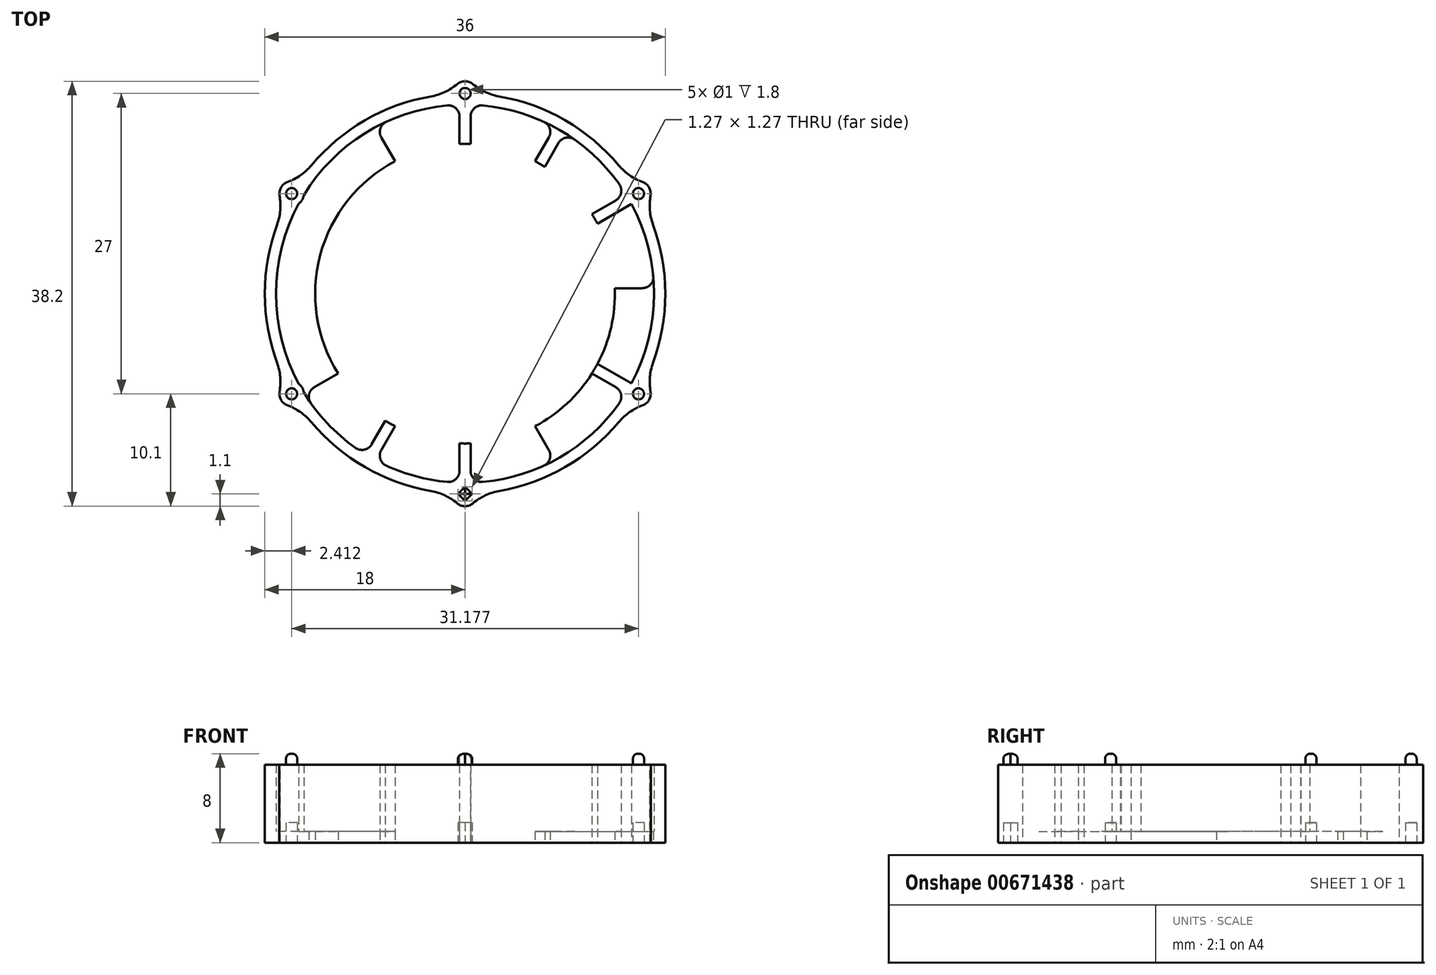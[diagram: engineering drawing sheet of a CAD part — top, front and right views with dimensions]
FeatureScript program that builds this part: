
annotation { "Feature Type Name" : "Feature", "Feature Type Description" : "" }
export const myFeature = defineFeature(function(context is Context, id is Id, definition is map)
    precondition{}
    {
        {
            var Q0;
            Q0=qCreatedBy(makeId("Top.planeOp"),FACE);
            var sketch = newSketch(context, id + "F0", { "sketchPlane" : qUnion([Q0])});
            skCircle(sketch, "E0", {"center": v(0, 0) * mm, "radius": 18 * mm});
            skCircle(sketch, "E1.0", {"center": v(0, 0) * mm, "radius": 17 * mm});
            skLineSegment(sketch, "E2.bottom", {"start": v(8.56, 15.83) * mm, "end": v(9.43, 15.33) * mm});
            skLineSegment(sketch, "E2.top", {"start": v(-9.43, -15.33) * mm, "end": v(-8.56, -15.83) * mm});
            skLineSegment(sketch, "E2.left", {"start": v(8.56, 15.83) * mm, "end": v(-9.43, -15.33) * mm});
            skLineSegment(sketch, "E2.right", {"start": v(9.43, 15.33) * mm, "end": v(-8.56, -15.83) * mm});
            skLineSegment(sketch, "E3.bottom", {"start": v(15.33, 9.43) * mm, "end": v(15.83, 8.56) * mm});
            skLineSegment(sketch, "E3.top", {"start": v(-15.83, -8.56) * mm, "end": v(-15.33, -9.43) * mm});
            skLineSegment(sketch, "E3.left", {"start": v(15.33, 9.43) * mm, "end": v(-15.83, -8.56) * mm});
            skLineSegment(sketch, "E3.right", {"start": v(15.83, 8.56) * mm, "end": v(-15.33, -9.43) * mm});
            skLineSegment(sketch, "E4", {"start": v(-38.35, 0) * mm, "end": v(39.17, 0) * mm, "construction": true});
            skLineSegment(sketch, "E5", {"start": v(0, 42.5) * mm, "end": v(0, -42.47) * mm, "construction": true});
            skLineSegment(sketch, "E6.bottom", {"start": v(-18, 0.5) * mm, "end": v(18, 0.5) * mm});
            skLineSegment(sketch, "E6.top", {"start": v(-18, -0.5) * mm, "end": v(18, -0.5) * mm});
            skLineSegment(sketch, "E6.left", {"start": v(-18, 0.5) * mm, "end": v(-18, -0.5) * mm});
            skLineSegment(sketch, "E6.right", {"start": v(18, 0.5) * mm, "end": v(18, -0.5) * mm});
            skLineSegment(sketch, "E7.bottom", {"start": v(-15.33, 9.43) * mm, "end": v(15.83, -8.56) * mm});
            skLineSegment(sketch, "E7.top", {"start": v(-15.83, 8.56) * mm, "end": v(15.33, -9.43) * mm});
            skLineSegment(sketch, "E7.left", {"start": v(-15.33, 9.43) * mm, "end": v(-15.83, 8.56) * mm});
            skLineSegment(sketch, "E7.right", {"start": v(15.83, -8.56) * mm, "end": v(15.33, -9.43) * mm});
            skLineSegment(sketch, "E8.bottom", {"start": v(-0.5, 18) * mm, "end": v(0.5, 18) * mm});
            skLineSegment(sketch, "E8.top", {"start": v(-0.5, -18) * mm, "end": v(0.5, -18) * mm});
            skLineSegment(sketch, "E8.left", {"start": v(-0.5, 18) * mm, "end": v(-0.5, -18) * mm});
            skLineSegment(sketch, "E8.right", {"start": v(0.5, 18) * mm, "end": v(0.5, -18) * mm});
            skLineSegment(sketch, "E9.bottom", {"start": v(-9.43, 15.33) * mm, "end": v(-8.56, 15.83) * mm});
            skLineSegment(sketch, "E9.top", {"start": v(8.56, -15.83) * mm, "end": v(9.43, -15.33) * mm});
            skLineSegment(sketch, "E9.left", {"start": v(-9.43, 15.33) * mm, "end": v(8.56, -15.83) * mm});
            skLineSegment(sketch, "E9.right", {"start": v(-8.56, 15.83) * mm, "end": v(9.43, -15.33) * mm});
            skCircle(sketch, "E10", {"center": v(0, 0) * mm, "radius": 13.47 * mm});
            skSolve(sketch);
        }
        {
            var Q0;
            Q0=qCreatedBy(makeId("Top.planeOp"),FACE);
            var sketch = newSketch(context, id + "F1", { "sketchPlane" : qUnion([Q0])});
            skCircle(sketch, "E11", {"center": v(0, 0) * mm, "radius": 18 * mm});
            skCircle(sketch, "E12", {"center": v(0, 0) * mm, "radius": 17 * mm});
            skSolve(sketch);
        }
        {
            var Q0;
            Q0=makeQuery(id+"F1.imprint","IMPRINT",FACE,{"disambiguationData":[TD([[makeQuery(id+"F1.imprint","IMPRINT",EDGE,{"derivedFrom":sQuery(id+"F1.wireOp",EDGE,"E11")}),1.0]])]});
            extrude(context, id + "F2", {"entities" : qUnion([Q0]), "depth" : 7 * mm, "offsetDistance" : 25 * mm});
        }
        {
            var Q0;
            {var subQ0=sQuery(id+"F0.wireOp",EDGE,"E8.left");var subQ1=sQuery(id+"F0.wireOp",EDGE,"E1.0");var subQ2=makeQuery(id+"F0.imprint","INTERSECT",VERTEX,{"disambiguationData":[OD(1.0)],"derivedFrom":[subQ1,subQ0]});Q0=makeQuery(id+"F0.imprint","IMPRINT",FACE,{"disambiguationData":[TD([[makeQuery(id+"F0.imprint","IMPRINT",EDGE,{"disambiguationData":[TD([[subQ2,-1.0]])],"derivedFrom":subQ1}),1.0]])]});}
            var Q1;
            {var subQ0=sQuery(id+"F0.wireOp",EDGE,"E8.right");var subQ1=sQuery(id+"F0.wireOp",EDGE,"E1.0");var subQ2=makeQuery(id+"F0.imprint","INTERSECT",VERTEX,{"disambiguationData":[OD(0.0)],"derivedFrom":[subQ1,subQ0]});Q1=makeQuery(id+"F0.imprint","IMPRINT",FACE,{"disambiguationData":[TD([[makeQuery(id+"F0.imprint","IMPRINT",EDGE,{"disambiguationData":[TD([[subQ2,-1.0]])],"derivedFrom":subQ1}),1.0]])]});}
            var Q2;
            {var subQ0=sQuery(id+"F0.wireOp",EDGE,"E3.right");var subQ1=sQuery(id+"F0.wireOp",EDGE,"E1.0");var subQ2=makeQuery(id+"F0.imprint","INTERSECT",VERTEX,{"disambiguationData":[OD(0.0)],"derivedFrom":[subQ1,subQ0]});Q2=makeQuery(id+"F0.imprint","IMPRINT",FACE,{"disambiguationData":[TD([[makeQuery(id+"F0.imprint","IMPRINT",EDGE,{"disambiguationData":[TD([[subQ2,-1.0]])],"derivedFrom":subQ1}),1.0]])]});}
            var Q3;
            {var subQ0=sQuery(id+"F0.wireOp",EDGE,"E7.top");var subQ1=sQuery(id+"F0.wireOp",EDGE,"E1.0");var subQ2=makeQuery(id+"F0.imprint","INTERSECT",VERTEX,{"disambiguationData":[OD(1.0)],"derivedFrom":[subQ1,subQ0]});Q3=makeQuery(id+"F0.imprint","IMPRINT",FACE,{"disambiguationData":[TD([[makeQuery(id+"F0.imprint","IMPRINT",EDGE,{"disambiguationData":[TD([[subQ2,-1.0]])],"derivedFrom":subQ1}),1.0]])]});}
            var Q4;
            {var subQ0=sQuery(id+"F0.wireOp",EDGE,"E2.left");var subQ1=sQuery(id+"F0.wireOp",EDGE,"E1.0");var subQ2=makeQuery(id+"F0.imprint","INTERSECT",VERTEX,{"disambiguationData":[OD(1.0)],"derivedFrom":[subQ1,subQ0]});Q4=makeQuery(id+"F0.imprint","IMPRINT",FACE,{"disambiguationData":[TD([[makeQuery(id+"F0.imprint","IMPRINT",EDGE,{"disambiguationData":[TD([[subQ2,-1.0]])],"derivedFrom":subQ1}),1.0]])]});}
            extrude(context, id + "F3", {"entities" : qUnion([Q0, Q1, Q2, Q3, Q4]), "operationType" : NewBodyOperationType.ADD, "depth" : 7 * mm, "offsetDistance" : 25 * mm});
        }
        {
            var Q0;
            Q0=makeQuery(id+"F1.imprint","IMPRINT",FACE,{"disambiguationData":[TD([[makeQuery(id+"F1.imprint","IMPRINT",EDGE,{"derivedFrom":sQuery(id+"F1.wireOp",EDGE,"E11")}),1.0]])]});
            var Q1;
            Q1=makeQuery(id+"F1.imprint","IMPRINT",FACE,{"disambiguationData":[TD([[makeQuery(id+"F1.imprint","IMPRINT",EDGE,{"derivedFrom":sQuery(id+"F1.wireOp",EDGE,"E12")}),1.0]])]});
            extrude(context, id + "F4", {"entities" : qUnion([Q0, Q1]), "operationType" : NewBodyOperationType.ADD, "depth" : 1 * mm, "offsetDistance" : 25 * mm});
        }
        {
            var Q0;
            Q0=qCreatedBy(makeId("Top.planeOp"),FACE);
            var sketch = newSketch(context, id + "F5", { "sketchPlane" : qUnion([Q0])});
            skCircle(sketch, "E13", {"center": v(0, 0) * mm, "radius": 18 * mm});
            skLineSegment(sketch, "E14", {"start": v(0, 18) * mm, "end": v(0, -18) * mm, "construction": true});
            skLineSegment(sketch, "E15", {"start": v(15.59, 9) * mm, "end": v(0, 0) * mm, "construction": true});
            skLineSegment(sketch, "E16", {"start": v(9, 15.59) * mm, "end": v(0, 0) * mm, "construction": true});
            skLineSegment(sketch, "E17", {"start": v(0, 0) * mm, "end": v(18, 0) * mm, "construction": true});
            skLineSegment(sketch, "E18", {"start": v(0, 0) * mm, "end": v(15.59, -9) * mm, "construction": true});
            skLineSegment(sketch, "E19", {"start": v(0, 0) * mm, "end": v(9, -15.59) * mm, "construction": true});
            skLineSegment(sketch, "E20", {"start": v(0, 0) * mm, "end": v(-9, 15.59) * mm, "construction": true});
            skLineSegment(sketch, "E21", {"start": v(0, 0) * mm, "end": v(-15.59, 9) * mm, "construction": true});
            skLineSegment(sketch, "E22", {"start": v(0, 0) * mm, "end": v(-18, 0) * mm, "construction": true});
            skLineSegment(sketch, "E23", {"start": v(0, 0) * mm, "end": v(-15.59, -9) * mm, "construction": true});
            skLineSegment(sketch, "E24", {"start": v(0, 0) * mm, "end": v(-9, -15.59) * mm, "construction": true});
            skCircle(sketch, "E25", {"center": v(0, 18) * mm, "radius": 1.1 * mm});
            skCircle(sketch, "E26", {"center": v(15.59, 9) * mm, "radius": 1.1 * mm});
            skCircle(sketch, "E27", {"center": v(15.59, -9) * mm, "radius": 1.1 * mm});
            skCircle(sketch, "E28", {"center": v(0, -18) * mm, "radius": 1.1 * mm});
            skCircle(sketch, "E29", {"center": v(-15.59, -9) * mm, "radius": 1.1 * mm});
            skCircle(sketch, "E30", {"center": v(-15.59, 9) * mm, "radius": 1.1 * mm});
            skCircle(sketch, "E31", {"center": v(-15.59, 9) * mm, "radius": 0.5 * mm});
            skCircle(sketch, "E32", {"center": v(0, 18) * mm, "radius": 0.5 * mm});
            skCircle(sketch, "E33", {"center": v(15.59, 9) * mm, "radius": 0.5 * mm});
            skCircle(sketch, "E34", {"center": v(15.59, -9) * mm, "radius": 0.5 * mm});
            skCircle(sketch, "E35", {"center": v(-15.59, -9) * mm, "radius": 0.5 * mm});
            skLineSegment(sketch, "E36.bottom", {"start": v(0.64, -18) * mm, "end": v(0, -18.64) * mm});
            skLineSegment(sketch, "E36.top", {"start": v(0, -17.36) * mm, "end": v(-0.64, -18) * mm});
            skLineSegment(sketch, "E36.left", {"start": v(0.64, -18) * mm, "end": v(0, -17.36) * mm});
            skLineSegment(sketch, "E36.right", {"start": v(0, -18.64) * mm, "end": v(-0.64, -18) * mm});
            skSolve(sketch);
        }
        {
            var Q0;
            {var subQ0=sQuery(id+"F5.wireOp",EDGE,"E30");var subQ1=sQuery(id+"F5.wireOp",EDGE,"E13");var subQ2=makeQuery(id+"F5.imprint","INTERSECT",VERTEX,{"disambiguationData":[OD(0.0)],"derivedFrom":[subQ1,subQ0]});Q0=makeQuery(id+"F5.imprint","IMPRINT",FACE,{"disambiguationData":[TD([[makeQuery(id+"F5.imprint","IMPRINT",EDGE,{"disambiguationData":[TD([[subQ2,-1.0]])],"derivedFrom":subQ1}),1.0]])]});}
            var Q1;
            {var subQ0=sQuery(id+"F5.wireOp",EDGE,"E30");var subQ1=sQuery(id+"F5.wireOp",EDGE,"E13");var subQ2=makeQuery(id+"F5.imprint","INTERSECT",VERTEX,{"disambiguationData":[OD(0.0)],"derivedFrom":[subQ1,subQ0]});Q1=makeQuery(id+"F5.imprint","IMPRINT",FACE,{"disambiguationData":[TD([[makeQuery(id+"F5.imprint","IMPRINT",EDGE,{"disambiguationData":[TD([[subQ2,-1.0]])],"derivedFrom":subQ1}),-1.0]])]});}
            var Q2;
            {var subQ0=sQuery(id+"F5.wireOp",EDGE,"E25");var subQ1=sQuery(id+"F5.wireOp",EDGE,"E13");var subQ2=makeQuery(id+"F5.imprint","INTERSECT",VERTEX,{"disambiguationData":[OD(0.0)],"derivedFrom":[subQ1,subQ0]});Q2=makeQuery(id+"F5.imprint","IMPRINT",FACE,{"disambiguationData":[TD([[makeQuery(id+"F5.imprint","IMPRINT",EDGE,{"disambiguationData":[TD([[subQ2,-1.0]])],"derivedFrom":subQ1}),1.0]])]});}
            var Q3;
            {var subQ0=sQuery(id+"F5.wireOp",EDGE,"E25");var subQ1=sQuery(id+"F5.wireOp",EDGE,"E13");var subQ2=makeQuery(id+"F5.imprint","INTERSECT",VERTEX,{"disambiguationData":[OD(0.0)],"derivedFrom":[subQ1,subQ0]});Q3=makeQuery(id+"F5.imprint","IMPRINT",FACE,{"disambiguationData":[TD([[makeQuery(id+"F5.imprint","IMPRINT",EDGE,{"disambiguationData":[TD([[subQ2,-1.0]])],"derivedFrom":subQ1}),-1.0]])]});}
            var Q4;
            {var subQ0=sQuery(id+"F5.wireOp",EDGE,"E26");var subQ1=sQuery(id+"F5.wireOp",EDGE,"E13");var subQ2=makeQuery(id+"F5.imprint","INTERSECT",VERTEX,{"disambiguationData":[OD(0.0)],"derivedFrom":[subQ1,subQ0]});Q4=makeQuery(id+"F5.imprint","IMPRINT",FACE,{"disambiguationData":[TD([[makeQuery(id+"F5.imprint","IMPRINT",EDGE,{"disambiguationData":[TD([[subQ2,-1.0]])],"derivedFrom":subQ1}),-1.0]])]});}
            var Q5;
            {var subQ0=sQuery(id+"F5.wireOp",EDGE,"E26");var subQ1=sQuery(id+"F5.wireOp",EDGE,"E13");var subQ2=makeQuery(id+"F5.imprint","INTERSECT",VERTEX,{"disambiguationData":[OD(0.0)],"derivedFrom":[subQ1,subQ0]});Q5=makeQuery(id+"F5.imprint","IMPRINT",FACE,{"disambiguationData":[TD([[makeQuery(id+"F5.imprint","IMPRINT",EDGE,{"disambiguationData":[TD([[subQ2,-1.0]])],"derivedFrom":subQ1}),1.0]])]});}
            var Q6;
            {var subQ0=sQuery(id+"F5.wireOp",EDGE,"E29");var subQ1=sQuery(id+"F5.wireOp",EDGE,"E13");var subQ2=makeQuery(id+"F5.imprint","INTERSECT",VERTEX,{"disambiguationData":[OD(0.0)],"derivedFrom":[subQ1,subQ0]});Q6=makeQuery(id+"F5.imprint","IMPRINT",FACE,{"disambiguationData":[TD([[makeQuery(id+"F5.imprint","IMPRINT",EDGE,{"disambiguationData":[TD([[subQ2,-1.0]])],"derivedFrom":subQ1}),1.0]])]});}
            var Q7;
            {var subQ0=sQuery(id+"F5.wireOp",EDGE,"E29");var subQ1=sQuery(id+"F5.wireOp",EDGE,"E13");var subQ2=makeQuery(id+"F5.imprint","INTERSECT",VERTEX,{"disambiguationData":[OD(0.0)],"derivedFrom":[subQ1,subQ0]});Q7=makeQuery(id+"F5.imprint","IMPRINT",FACE,{"disambiguationData":[TD([[makeQuery(id+"F5.imprint","IMPRINT",EDGE,{"disambiguationData":[TD([[subQ2,-1.0]])],"derivedFrom":subQ1}),-1.0]])]});}
            var Q8;
            {var subQ3=sQuery(id+"F5.wireOp",EDGE,"E13");var subQ5=sQuery(id+"F5.wireOp",EDGE,"E28");var subQ6=makeQuery(id+"F5.imprint","INTERSECT",VERTEX,{"disambiguationData":[OD(0.0)],"derivedFrom":[subQ3,subQ5]});Q8=makeQuery(id+"F5.imprint","IMPRINT",FACE,{"disambiguationData":[TD([[makeQuery(id+"F5.imprint","IMPRINT",EDGE,{"disambiguationData":[TD([[subQ6,-1.0]])],"derivedFrom":subQ3}),1.0]])]});}
            var Q9;
            {var subQ6=sQuery(id+"F5.wireOp",EDGE,"E36.bottom");Q9=makeQuery(id+"F5.imprint","IMPRINT",FACE,{"disambiguationData":[TD([[makeQuery(id+"F5.imprint","IMPRINT",EDGE,{"derivedFrom":subQ6}),1.0]])]});}
            var Q10;
            {var subQ0=sQuery(id+"F5.wireOp",EDGE,"E27");var subQ1=sQuery(id+"F5.wireOp",EDGE,"E13");var subQ2=makeQuery(id+"F5.imprint","INTERSECT",VERTEX,{"disambiguationData":[OD(0.0)],"derivedFrom":[subQ1,subQ0]});Q10=makeQuery(id+"F5.imprint","IMPRINT",FACE,{"disambiguationData":[TD([[makeQuery(id+"F5.imprint","IMPRINT",EDGE,{"disambiguationData":[TD([[subQ2,-1.0]])],"derivedFrom":subQ1}),-1.0]])]});}
            var Q11;
            {var subQ0=sQuery(id+"F5.wireOp",EDGE,"E27");var subQ1=sQuery(id+"F5.wireOp",EDGE,"E13");var subQ2=makeQuery(id+"F5.imprint","INTERSECT",VERTEX,{"disambiguationData":[OD(0.0)],"derivedFrom":[subQ1,subQ0]});Q11=makeQuery(id+"F5.imprint","IMPRINT",FACE,{"disambiguationData":[TD([[makeQuery(id+"F5.imprint","IMPRINT",EDGE,{"disambiguationData":[TD([[subQ2,-1.0]])],"derivedFrom":subQ1}),1.0]])]});}
            var Q12;
            {var subQ0=sQuery(id+"F5.wireOp",EDGE,"E31");var subQ1=sQuery(id+"F5.wireOp",EDGE,"E13");var subQ2=makeQuery(id+"F5.imprint","INTERSECT",VERTEX,{"disambiguationData":[OD(0.0)],"derivedFrom":[subQ1,subQ0]});Q12=makeQuery(id+"F5.imprint","IMPRINT",FACE,{"disambiguationData":[TD([[makeQuery(id+"F5.imprint","IMPRINT",EDGE,{"disambiguationData":[TD([[subQ2,-1.0]])],"derivedFrom":subQ1}),1.0]])]});}
            var Q13;
            {var subQ0=sQuery(id+"F5.wireOp",EDGE,"E31");var subQ1=sQuery(id+"F5.wireOp",EDGE,"E13");var subQ2=makeQuery(id+"F5.imprint","INTERSECT",VERTEX,{"disambiguationData":[OD(0.0)],"derivedFrom":[subQ1,subQ0]});Q13=makeQuery(id+"F5.imprint","IMPRINT",FACE,{"disambiguationData":[TD([[makeQuery(id+"F5.imprint","IMPRINT",EDGE,{"disambiguationData":[TD([[subQ2,-1.0]])],"derivedFrom":subQ1}),-1.0]])]});}
            var Q14;
            {var subQ0=sQuery(id+"F5.wireOp",EDGE,"E32");var subQ1=sQuery(id+"F5.wireOp",EDGE,"E13");var subQ2=makeQuery(id+"F5.imprint","INTERSECT",VERTEX,{"disambiguationData":[OD(0.0)],"derivedFrom":[subQ1,subQ0]});Q14=makeQuery(id+"F5.imprint","IMPRINT",FACE,{"disambiguationData":[TD([[makeQuery(id+"F5.imprint","IMPRINT",EDGE,{"disambiguationData":[TD([[subQ2,-1.0]])],"derivedFrom":subQ1}),-1.0]])]});}
            var Q15;
            {var subQ0=sQuery(id+"F5.wireOp",EDGE,"E32");var subQ1=sQuery(id+"F5.wireOp",EDGE,"E13");var subQ2=makeQuery(id+"F5.imprint","INTERSECT",VERTEX,{"disambiguationData":[OD(0.0)],"derivedFrom":[subQ1,subQ0]});Q15=makeQuery(id+"F5.imprint","IMPRINT",FACE,{"disambiguationData":[TD([[makeQuery(id+"F5.imprint","IMPRINT",EDGE,{"disambiguationData":[TD([[subQ2,-1.0]])],"derivedFrom":subQ1}),1.0]])]});}
            var Q16;
            {var subQ0=sQuery(id+"F5.wireOp",EDGE,"E33");var subQ1=sQuery(id+"F5.wireOp",EDGE,"E13");var subQ2=makeQuery(id+"F5.imprint","INTERSECT",VERTEX,{"disambiguationData":[OD(0.0)],"derivedFrom":[subQ1,subQ0]});Q16=makeQuery(id+"F5.imprint","IMPRINT",FACE,{"disambiguationData":[TD([[makeQuery(id+"F5.imprint","IMPRINT",EDGE,{"disambiguationData":[TD([[subQ2,-1.0]])],"derivedFrom":subQ1}),-1.0]])]});}
            var Q17;
            {var subQ0=sQuery(id+"F5.wireOp",EDGE,"E33");var subQ1=sQuery(id+"F5.wireOp",EDGE,"E13");var subQ2=makeQuery(id+"F5.imprint","INTERSECT",VERTEX,{"disambiguationData":[OD(0.0)],"derivedFrom":[subQ1,subQ0]});Q17=makeQuery(id+"F5.imprint","IMPRINT",FACE,{"disambiguationData":[TD([[makeQuery(id+"F5.imprint","IMPRINT",EDGE,{"disambiguationData":[TD([[subQ2,-1.0]])],"derivedFrom":subQ1}),1.0]])]});}
            var Q18;
            {var subQ0=sQuery(id+"F5.wireOp",EDGE,"E34");var subQ1=sQuery(id+"F5.wireOp",EDGE,"E13");var subQ2=makeQuery(id+"F5.imprint","INTERSECT",VERTEX,{"disambiguationData":[OD(0.0)],"derivedFrom":[subQ1,subQ0]});Q18=makeQuery(id+"F5.imprint","IMPRINT",FACE,{"disambiguationData":[TD([[makeQuery(id+"F5.imprint","IMPRINT",EDGE,{"disambiguationData":[TD([[subQ2,-1.0]])],"derivedFrom":subQ1}),-1.0]])]});}
            var Q19;
            {var subQ0=sQuery(id+"F5.wireOp",EDGE,"E34");var subQ1=sQuery(id+"F5.wireOp",EDGE,"E13");var subQ2=makeQuery(id+"F5.imprint","INTERSECT",VERTEX,{"disambiguationData":[OD(0.0)],"derivedFrom":[subQ1,subQ0]});Q19=makeQuery(id+"F5.imprint","IMPRINT",FACE,{"disambiguationData":[TD([[makeQuery(id+"F5.imprint","IMPRINT",EDGE,{"disambiguationData":[TD([[subQ2,-1.0]])],"derivedFrom":subQ1}),1.0]])]});}
            var Q20;
            {var subQ1=sQuery(id+"F5.wireOp",EDGE,"E36.bottom");Q20=makeQuery(id+"F5.imprint","IMPRINT",FACE,{"disambiguationData":[TD([[makeQuery(id+"F5.imprint","IMPRINT",EDGE,{"derivedFrom":subQ1}),-1.0]])]});}
            var Q21;
            {var subQ0=sQuery(id+"F5.wireOp",EDGE,"E35");var subQ1=sQuery(id+"F5.wireOp",EDGE,"E13");var subQ2=makeQuery(id+"F5.imprint","INTERSECT",VERTEX,{"disambiguationData":[OD(0.0)],"derivedFrom":[subQ1,subQ0]});Q21=makeQuery(id+"F5.imprint","IMPRINT",FACE,{"disambiguationData":[TD([[makeQuery(id+"F5.imprint","IMPRINT",EDGE,{"disambiguationData":[TD([[subQ2,-1.0]])],"derivedFrom":subQ1}),-1.0]])]});}
            var Q22;
            {var subQ0=sQuery(id+"F5.wireOp",EDGE,"E35");var subQ1=sQuery(id+"F5.wireOp",EDGE,"E13");var subQ2=makeQuery(id+"F5.imprint","INTERSECT",VERTEX,{"disambiguationData":[OD(0.0)],"derivedFrom":[subQ1,subQ0]});Q22=makeQuery(id+"F5.imprint","IMPRINT",FACE,{"disambiguationData":[TD([[makeQuery(id+"F5.imprint","IMPRINT",EDGE,{"disambiguationData":[TD([[subQ2,-1.0]])],"derivedFrom":subQ1}),1.0]])]});}
            var Q23;
            {var subQ0=sQuery(id+"F5.wireOp",EDGE,"E36.top");var subQ1=sQuery(id+"F5.wireOp",EDGE,"E13");var subQ2=makeQuery(id+"F5.imprint","INTERSECT",VERTEX,{"derivedFrom":[subQ1,subQ0]});Q23=makeQuery(id+"F5.imprint","IMPRINT",FACE,{"disambiguationData":[TD([[makeQuery(id+"F5.imprint","IMPRINT",EDGE,{"disambiguationData":[TD([[subQ2,-1.0]])],"derivedFrom":subQ1}),1.0]])]});}
            extrude(context, id + "F6", {"entities" : qUnion([Q0, Q1, Q2, Q3, Q4, Q5, Q6, Q7, Q8, Q9, Q10, Q11, Q12, Q13, Q14, Q15, Q16, Q17, Q18, Q19, Q20, Q21, Q22, Q23]), "operationType" : NewBodyOperationType.ADD, "depth" : 7 * mm, "offsetDistance" : 25 * mm});
        }
        {
            var Q0;
            {var subQ0=sQuery(id+"F0.wireOp",EDGE,"E8.right");var subQ1=sQuery(id+"F0.wireOp",EDGE,"E1.0");Q0=makeQuery(id+"F3.opExtrude","SWEPT_EDGE",EDGE,{"disambiguationData":[OSD([subQ1,subQ0]),TDD([makeQuery(id+"F0.imprint","INTERSECT",VERTEX,{"disambiguationData":[OD(1.0)],"derivedFrom":[subQ1,subQ0]})])]});}
            var Q1;
            {var subQ0=sQuery(id+"F0.wireOp",EDGE,"E2.left");var subQ1=sQuery(id+"F0.wireOp",EDGE,"E1.0");Q1=makeQuery(id+"F3.opExtrude","SWEPT_EDGE",EDGE,{"disambiguationData":[OSD([subQ1,subQ0]),TDD([makeQuery(id+"F0.imprint","INTERSECT",VERTEX,{"disambiguationData":[OD(1.0)],"derivedFrom":[subQ1,subQ0]})])]});}
            var Q2;
            {var subQ0=sQuery(id+"F0.wireOp",EDGE,"E3.left");var subQ1=sQuery(id+"F0.wireOp",EDGE,"E1.0");Q2=makeQuery(id+"F3.opExtrude","SWEPT_EDGE",EDGE,{"disambiguationData":[OSD([subQ1,subQ0]),TDD([makeQuery(id+"F0.imprint","INTERSECT",VERTEX,{"disambiguationData":[OD(1.0)],"derivedFrom":[subQ1,subQ0]})])]});}
            var Q3;
            {var subQ0=sQuery(id+"F0.wireOp",EDGE,"E6.bottom");var subQ1=sQuery(id+"F0.wireOp",EDGE,"E1.0");Q3=makeQuery(id+"F3.opExtrude","SWEPT_EDGE",EDGE,{"disambiguationData":[OSD([subQ1,subQ0]),TDD([makeQuery(id+"F0.imprint","INTERSECT",VERTEX,{"disambiguationData":[OD(1.0)],"derivedFrom":[subQ1,subQ0]})])]});}
            var Q4;
            {var subQ0=sQuery(id+"F0.wireOp",EDGE,"E9.right");var subQ1=sQuery(id+"F0.wireOp",EDGE,"E1.0");Q4=makeQuery(id+"F3.opExtrude","SWEPT_EDGE",EDGE,{"disambiguationData":[OSD([subQ1,subQ0]),TDD([makeQuery(id+"F0.imprint","INTERSECT",VERTEX,{"disambiguationData":[OD(1.0)],"derivedFrom":[subQ1,subQ0]})])]});}
            var Q5;
            {var subQ0=sQuery(id+"F0.wireOp",EDGE,"E7.bottom");var subQ1=sQuery(id+"F0.wireOp",EDGE,"E1.0");Q5=makeQuery(id+"F3.opExtrude","SWEPT_EDGE",EDGE,{"disambiguationData":[OSD([subQ1,subQ0]),TDD([makeQuery(id+"F0.imprint","INTERSECT",VERTEX,{"disambiguationData":[OD(1.0)],"derivedFrom":[subQ1,subQ0]})])]});}
            var Q6;
            {var subQ0=sQuery(id+"F0.wireOp",EDGE,"E8.left");var subQ1=sQuery(id+"F0.wireOp",EDGE,"E1.0");Q6=makeQuery(id+"F3.opExtrude","SWEPT_EDGE",EDGE,{"disambiguationData":[OSD([subQ1,subQ0]),TDD([makeQuery(id+"F0.imprint","INTERSECT",VERTEX,{"disambiguationData":[OD(0.0)],"derivedFrom":[subQ1,subQ0]})])]});}
            var Q7;
            {var subQ0=sQuery(id+"F0.wireOp",EDGE,"E2.left");var subQ1=sQuery(id+"F0.wireOp",EDGE,"E1.0");Q7=makeQuery(id+"F3.opExtrude","SWEPT_EDGE",EDGE,{"disambiguationData":[OSD([subQ1,subQ0]),TDD([makeQuery(id+"F0.imprint","INTERSECT",VERTEX,{"disambiguationData":[OD(0.0)],"derivedFrom":[subQ1,subQ0]})])]});}
            var Q8;
            {var subQ0=sQuery(id+"F0.wireOp",EDGE,"E3.left");var subQ1=sQuery(id+"F0.wireOp",EDGE,"E1.0");Q8=makeQuery(id+"F3.opExtrude","SWEPT_EDGE",EDGE,{"disambiguationData":[OSD([subQ1,subQ0]),TDD([makeQuery(id+"F0.imprint","INTERSECT",VERTEX,{"disambiguationData":[OD(0.0)],"derivedFrom":[subQ1,subQ0]})])]});}
            var Q9;
            {var subQ0=sQuery(id+"F0.wireOp",EDGE,"E6.top");var subQ1=sQuery(id+"F0.wireOp",EDGE,"E1.0");Q9=makeQuery(id+"F3.opExtrude","SWEPT_EDGE",EDGE,{"disambiguationData":[OSD([subQ1,subQ0]),TDD([makeQuery(id+"F0.imprint","INTERSECT",VERTEX,{"disambiguationData":[OD(1.0)],"derivedFrom":[subQ1,subQ0]})])]});}
            var Q10;
            {var subQ0=sQuery(id+"F0.wireOp",EDGE,"E7.top");var subQ1=sQuery(id+"F0.wireOp",EDGE,"E1.0");Q10=makeQuery(id+"F3.opExtrude","SWEPT_EDGE",EDGE,{"disambiguationData":[OSD([subQ1,subQ0]),TDD([makeQuery(id+"F0.imprint","INTERSECT",VERTEX,{"disambiguationData":[OD(0.0)],"derivedFrom":[subQ1,subQ0]})])]});}
            var Q11;
            {var subQ0=sQuery(id+"F0.wireOp",EDGE,"E6.top");var subQ1=sQuery(id+"F0.wireOp",EDGE,"E1.0");Q11=makeQuery(id+"F3.opExtrude","SWEPT_EDGE",EDGE,{"disambiguationData":[OSD([subQ1,subQ0]),TDD([makeQuery(id+"F0.imprint","INTERSECT",VERTEX,{"disambiguationData":[OD(0.0)],"derivedFrom":[subQ1,subQ0]})])]});}
            var Q12;
            {var subQ0=sQuery(id+"F0.wireOp",EDGE,"E9.left");var subQ1=sQuery(id+"F0.wireOp",EDGE,"E1.0");Q12=makeQuery(id+"F3.opExtrude","SWEPT_EDGE",EDGE,{"disambiguationData":[OSD([subQ1,subQ0]),TDD([makeQuery(id+"F0.imprint","INTERSECT",VERTEX,{"disambiguationData":[OD(0.0)],"derivedFrom":[subQ1,subQ0]})])]});}
            var Q13;
            {var subQ0=sQuery(id+"F0.wireOp",EDGE,"E8.right");var subQ1=sQuery(id+"F0.wireOp",EDGE,"E1.0");Q13=makeQuery(id+"F3.opExtrude","SWEPT_EDGE",EDGE,{"disambiguationData":[OSD([subQ1,subQ0]),TDD([makeQuery(id+"F0.imprint","INTERSECT",VERTEX,{"disambiguationData":[OD(0.0)],"derivedFrom":[subQ1,subQ0]})])]});}
            var Q14;
            {var subQ0=sQuery(id+"F0.wireOp",EDGE,"E7.bottom");var subQ1=sQuery(id+"F0.wireOp",EDGE,"E1.0");Q14=makeQuery(id+"F3.opExtrude","SWEPT_EDGE",EDGE,{"disambiguationData":[OSD([subQ1,subQ0]),TDD([makeQuery(id+"F0.imprint","INTERSECT",VERTEX,{"disambiguationData":[OD(0.0)],"derivedFrom":[subQ1,subQ0]})])]});}
            var Q15;
            {var subQ0=sQuery(id+"F0.wireOp",EDGE,"E9.right");var subQ1=sQuery(id+"F0.wireOp",EDGE,"E1.0");Q15=makeQuery(id+"F3.opExtrude","SWEPT_EDGE",EDGE,{"disambiguationData":[OSD([subQ1,subQ0]),TDD([makeQuery(id+"F0.imprint","INTERSECT",VERTEX,{"disambiguationData":[OD(0.0)],"derivedFrom":[subQ1,subQ0]})])]});}
            var Q16;
            {var subQ0=sQuery(id+"F0.wireOp",EDGE,"E3.right");var subQ1=sQuery(id+"F0.wireOp",EDGE,"E1.0");Q16=makeQuery(id+"F3.opExtrude","SWEPT_EDGE",EDGE,{"disambiguationData":[OSD([subQ1,subQ0]),TDD([makeQuery(id+"F0.imprint","INTERSECT",VERTEX,{"disambiguationData":[OD(1.0)],"derivedFrom":[subQ1,subQ0]})])]});}
            var Q17;
            {var subQ0=sQuery(id+"F0.wireOp",EDGE,"E2.right");var subQ1=sQuery(id+"F0.wireOp",EDGE,"E1.0");Q17=makeQuery(id+"F3.opExtrude","SWEPT_EDGE",EDGE,{"disambiguationData":[OSD([subQ1,subQ0]),TDD([makeQuery(id+"F0.imprint","INTERSECT",VERTEX,{"disambiguationData":[OD(1.0)],"derivedFrom":[subQ1,subQ0]})])]});}
            var Q18;
            {var subQ0=sQuery(id+"F0.wireOp",EDGE,"E3.right");var subQ1=sQuery(id+"F0.wireOp",EDGE,"E1.0");Q18=makeQuery(id+"F3.opExtrude","SWEPT_EDGE",EDGE,{"disambiguationData":[OSD([subQ1,subQ0]),TDD([makeQuery(id+"F0.imprint","INTERSECT",VERTEX,{"disambiguationData":[OD(0.0)],"derivedFrom":[subQ1,subQ0]})])]});}
            var Q19;
            {var subQ0=sQuery(id+"F0.wireOp",EDGE,"E2.right");var subQ1=sQuery(id+"F0.wireOp",EDGE,"E1.0");Q19=makeQuery(id+"F3.opExtrude","SWEPT_EDGE",EDGE,{"disambiguationData":[OSD([subQ1,subQ0]),TDD([makeQuery(id+"F0.imprint","INTERSECT",VERTEX,{"disambiguationData":[OD(0.0)],"derivedFrom":[subQ1,subQ0]})])]});}
            var Q20;
            {var subQ0=sQuery(id+"F0.wireOp",EDGE,"E8.left");var subQ1=sQuery(id+"F0.wireOp",EDGE,"E1.0");Q20=makeQuery(id+"F3.opExtrude","SWEPT_EDGE",EDGE,{"disambiguationData":[OSD([subQ1,subQ0]),TDD([makeQuery(id+"F0.imprint","INTERSECT",VERTEX,{"disambiguationData":[OD(1.0)],"derivedFrom":[subQ1,subQ0]})])]});}
            var Q21;
            {var subQ0=sQuery(id+"F0.wireOp",EDGE,"E9.left");var subQ1=sQuery(id+"F0.wireOp",EDGE,"E1.0");Q21=makeQuery(id+"F3.opExtrude","SWEPT_EDGE",EDGE,{"disambiguationData":[OSD([subQ1,subQ0]),TDD([makeQuery(id+"F0.imprint","INTERSECT",VERTEX,{"disambiguationData":[OD(1.0)],"derivedFrom":[subQ1,subQ0]})])]});}
            var Q22;
            {var subQ0=sQuery(id+"F0.wireOp",EDGE,"E7.top");var subQ1=sQuery(id+"F0.wireOp",EDGE,"E1.0");Q22=makeQuery(id+"F3.opExtrude","SWEPT_EDGE",EDGE,{"disambiguationData":[OSD([subQ1,subQ0]),TDD([makeQuery(id+"F0.imprint","INTERSECT",VERTEX,{"disambiguationData":[OD(1.0)],"derivedFrom":[subQ1,subQ0]})])]});}
            var Q23;
            {var subQ0=sQuery(id+"F0.wireOp",EDGE,"E6.bottom");var subQ1=sQuery(id+"F0.wireOp",EDGE,"E1.0");Q23=makeQuery(id+"F3.opExtrude","SWEPT_EDGE",EDGE,{"disambiguationData":[OSD([subQ1,subQ0]),TDD([makeQuery(id+"F0.imprint","INTERSECT",VERTEX,{"disambiguationData":[OD(0.0)],"derivedFrom":[subQ1,subQ0]})])]});}
            fillet(context, id + "F7", {"entities" : qUnion([Q0, Q1, Q2, Q3, Q4, Q5, Q6, Q7, Q8, Q9, Q10, Q11, Q12, Q13, Q14, Q15, Q16, Q17, Q18, Q19, Q20, Q21, Q22, Q23]), "radius" : 1 * mm, "tangentPropagation" : true, "allowEdgeOverflow" : false});
        }
        {
            var Q0;
            Q0=makeQuery(id+"F6.boolean.opBoolean","INTERSECT",EDGE,{"disambiguationData":[OD(0.0)],"derivedFrom":[makeQuery(id+"F2.opExtrude","SWEPT_FACE",FACE,{"disambiguationData":[OSD([sQuery(id+"F1.wireOp",EDGE,"E11")])]}),makeQuery(id+"F6.opExtrude","SWEPT_FACE",FACE,{"disambiguationData":[OSD([sQuery(id+"F5.wireOp",EDGE,"E30")])]})]});
            var Q1;
            Q1=makeQuery(id+"F6.boolean.opBoolean","INTERSECT",EDGE,{"disambiguationData":[OD(1.0)],"derivedFrom":[makeQuery(id+"F2.opExtrude","SWEPT_FACE",FACE,{"disambiguationData":[OSD([sQuery(id+"F1.wireOp",EDGE,"E11")])]}),makeQuery(id+"F6.opExtrude","SWEPT_FACE",FACE,{"disambiguationData":[OSD([sQuery(id+"F5.wireOp",EDGE,"E30")])]})]});
            var Q2;
            Q2=makeQuery(id+"F6.boolean.opBoolean","INTERSECT",EDGE,{"disambiguationData":[OD(1.0)],"derivedFrom":[makeQuery(id+"F2.opExtrude","SWEPT_FACE",FACE,{"disambiguationData":[OSD([sQuery(id+"F1.wireOp",EDGE,"E11")])]}),makeQuery(id+"F6.opExtrude","SWEPT_FACE",FACE,{"disambiguationData":[OSD([sQuery(id+"F5.wireOp",EDGE,"E25")])]})]});
            var Q3;
            Q3=makeQuery(id+"F6.boolean.opBoolean","INTERSECT",EDGE,{"disambiguationData":[OD(1.0)],"derivedFrom":[makeQuery(id+"F2.opExtrude","SWEPT_FACE",FACE,{"disambiguationData":[OSD([sQuery(id+"F1.wireOp",EDGE,"E11")])]}),makeQuery(id+"F6.opExtrude","SWEPT_FACE",FACE,{"disambiguationData":[OSD([sQuery(id+"F5.wireOp",EDGE,"E29")])]})]});
            var Q4;
            Q4=makeQuery(id+"F6.boolean.opBoolean","INTERSECT",EDGE,{"disambiguationData":[OD(0.0)],"derivedFrom":[makeQuery(id+"F2.opExtrude","SWEPT_FACE",FACE,{"disambiguationData":[OSD([sQuery(id+"F1.wireOp",EDGE,"E11")])]}),makeQuery(id+"F6.opExtrude","SWEPT_FACE",FACE,{"disambiguationData":[OSD([sQuery(id+"F5.wireOp",EDGE,"E29")])]})]});
            var Q5;
            Q5=makeQuery(id+"F6.boolean.opBoolean","INTERSECT",EDGE,{"disambiguationData":[OD(1.0)],"derivedFrom":[makeQuery(id+"F2.opExtrude","SWEPT_FACE",FACE,{"disambiguationData":[OSD([sQuery(id+"F1.wireOp",EDGE,"E11")])]}),makeQuery(id+"F6.opExtrude","SWEPT_FACE",FACE,{"disambiguationData":[OSD([sQuery(id+"F5.wireOp",EDGE,"E28")])]})]});
            var Q6;
            Q6=makeQuery(id+"F6.boolean.opBoolean","INTERSECT",EDGE,{"disambiguationData":[OD(0.0)],"derivedFrom":[makeQuery(id+"F2.opExtrude","SWEPT_FACE",FACE,{"disambiguationData":[OSD([sQuery(id+"F1.wireOp",EDGE,"E11")])]}),makeQuery(id+"F6.opExtrude","SWEPT_FACE",FACE,{"disambiguationData":[OSD([sQuery(id+"F5.wireOp",EDGE,"E28")])]})]});
            var Q7;
            Q7=makeQuery(id+"F6.boolean.opBoolean","INTERSECT",EDGE,{"disambiguationData":[OD(1.0)],"derivedFrom":[makeQuery(id+"F2.opExtrude","SWEPT_FACE",FACE,{"disambiguationData":[OSD([sQuery(id+"F1.wireOp",EDGE,"E11")])]}),makeQuery(id+"F6.opExtrude","SWEPT_FACE",FACE,{"disambiguationData":[OSD([sQuery(id+"F5.wireOp",EDGE,"E27")])]})]});
            var Q8;
            Q8=makeQuery(id+"F6.boolean.opBoolean","INTERSECT",EDGE,{"disambiguationData":[OD(0.0)],"derivedFrom":[makeQuery(id+"F2.opExtrude","SWEPT_FACE",FACE,{"disambiguationData":[OSD([sQuery(id+"F1.wireOp",EDGE,"E11")])]}),makeQuery(id+"F6.opExtrude","SWEPT_FACE",FACE,{"disambiguationData":[OSD([sQuery(id+"F5.wireOp",EDGE,"E27")])]})]});
            var Q9;
            Q9=makeQuery(id+"F6.boolean.opBoolean","INTERSECT",EDGE,{"disambiguationData":[OD(1.0)],"derivedFrom":[makeQuery(id+"F2.opExtrude","SWEPT_FACE",FACE,{"disambiguationData":[OSD([sQuery(id+"F1.wireOp",EDGE,"E11")])]}),makeQuery(id+"F6.opExtrude","SWEPT_FACE",FACE,{"disambiguationData":[OSD([sQuery(id+"F5.wireOp",EDGE,"E26")])]})]});
            var Q10;
            Q10=makeQuery(id+"F6.boolean.opBoolean","INTERSECT",EDGE,{"disambiguationData":[OD(0.0)],"derivedFrom":[makeQuery(id+"F2.opExtrude","SWEPT_FACE",FACE,{"disambiguationData":[OSD([sQuery(id+"F1.wireOp",EDGE,"E11")])]}),makeQuery(id+"F6.opExtrude","SWEPT_FACE",FACE,{"disambiguationData":[OSD([sQuery(id+"F5.wireOp",EDGE,"E26")])]})]});
            var Q11;
            Q11=makeQuery(id+"F6.boolean.opBoolean","INTERSECT",EDGE,{"disambiguationData":[OD(0.0)],"derivedFrom":[makeQuery(id+"F2.opExtrude","SWEPT_FACE",FACE,{"disambiguationData":[OSD([sQuery(id+"F1.wireOp",EDGE,"E11")])]}),makeQuery(id+"F6.opExtrude","SWEPT_FACE",FACE,{"disambiguationData":[OSD([sQuery(id+"F5.wireOp",EDGE,"E25")])]})]});
            fillet(context, id + "F8", {"entities" : qUnion([Q0, Q1, Q2, Q3, Q4, Q5, Q6, Q7, Q8, Q9, Q10, Q11]), "radius" : 5 * mm, "tangentPropagation" : true, "allowEdgeOverflow" : false});
        }
        {
            var Q0;
            {var subQ0=sQuery(id+"F5.wireOp",EDGE,"E31");var subQ1=sQuery(id+"F5.wireOp",EDGE,"E13");var subQ2=makeQuery(id+"F5.imprint","INTERSECT",VERTEX,{"disambiguationData":[OD(0.0)],"derivedFrom":[subQ1,subQ0]});Q0=makeQuery(id+"F5.imprint","IMPRINT",FACE,{"disambiguationData":[TD([[makeQuery(id+"F5.imprint","IMPRINT",EDGE,{"disambiguationData":[TD([[subQ2,-1.0]])],"derivedFrom":subQ1}),-1.0]])]});}
            var Q1;
            {var subQ0=sQuery(id+"F5.wireOp",EDGE,"E31");var subQ1=sQuery(id+"F5.wireOp",EDGE,"E13");var subQ2=makeQuery(id+"F5.imprint","INTERSECT",VERTEX,{"disambiguationData":[OD(0.0)],"derivedFrom":[subQ1,subQ0]});Q1=makeQuery(id+"F5.imprint","IMPRINT",FACE,{"disambiguationData":[TD([[makeQuery(id+"F5.imprint","IMPRINT",EDGE,{"disambiguationData":[TD([[subQ2,-1.0]])],"derivedFrom":subQ1}),1.0]])]});}
            var Q2;
            {var subQ0=sQuery(id+"F5.wireOp",EDGE,"E32");var subQ1=sQuery(id+"F5.wireOp",EDGE,"E13");var subQ2=makeQuery(id+"F5.imprint","INTERSECT",VERTEX,{"disambiguationData":[OD(0.0)],"derivedFrom":[subQ1,subQ0]});Q2=makeQuery(id+"F5.imprint","IMPRINT",FACE,{"disambiguationData":[TD([[makeQuery(id+"F5.imprint","IMPRINT",EDGE,{"disambiguationData":[TD([[subQ2,-1.0]])],"derivedFrom":subQ1}),-1.0]])]});}
            var Q3;
            {var subQ0=sQuery(id+"F5.wireOp",EDGE,"E32");var subQ1=sQuery(id+"F5.wireOp",EDGE,"E13");var subQ2=makeQuery(id+"F5.imprint","INTERSECT",VERTEX,{"disambiguationData":[OD(0.0)],"derivedFrom":[subQ1,subQ0]});Q3=makeQuery(id+"F5.imprint","IMPRINT",FACE,{"disambiguationData":[TD([[makeQuery(id+"F5.imprint","IMPRINT",EDGE,{"disambiguationData":[TD([[subQ2,-1.0]])],"derivedFrom":subQ1}),1.0]])]});}
            var Q4;
            {var subQ0=sQuery(id+"F5.wireOp",EDGE,"E33");var subQ1=sQuery(id+"F5.wireOp",EDGE,"E13");var subQ2=makeQuery(id+"F5.imprint","INTERSECT",VERTEX,{"disambiguationData":[OD(0.0)],"derivedFrom":[subQ1,subQ0]});Q4=makeQuery(id+"F5.imprint","IMPRINT",FACE,{"disambiguationData":[TD([[makeQuery(id+"F5.imprint","IMPRINT",EDGE,{"disambiguationData":[TD([[subQ2,-1.0]])],"derivedFrom":subQ1}),1.0]])]});}
            var Q5;
            {var subQ0=sQuery(id+"F5.wireOp",EDGE,"E33");var subQ1=sQuery(id+"F5.wireOp",EDGE,"E13");var subQ2=makeQuery(id+"F5.imprint","INTERSECT",VERTEX,{"disambiguationData":[OD(0.0)],"derivedFrom":[subQ1,subQ0]});Q5=makeQuery(id+"F5.imprint","IMPRINT",FACE,{"disambiguationData":[TD([[makeQuery(id+"F5.imprint","IMPRINT",EDGE,{"disambiguationData":[TD([[subQ2,-1.0]])],"derivedFrom":subQ1}),-1.0]])]});}
            var Q6;
            {var subQ0=sQuery(id+"F5.wireOp",EDGE,"E34");var subQ1=sQuery(id+"F5.wireOp",EDGE,"E13");var subQ2=makeQuery(id+"F5.imprint","INTERSECT",VERTEX,{"disambiguationData":[OD(0.0)],"derivedFrom":[subQ1,subQ0]});Q6=makeQuery(id+"F5.imprint","IMPRINT",FACE,{"disambiguationData":[TD([[makeQuery(id+"F5.imprint","IMPRINT",EDGE,{"disambiguationData":[TD([[subQ2,-1.0]])],"derivedFrom":subQ1}),1.0]])]});}
            var Q7;
            {var subQ0=sQuery(id+"F5.wireOp",EDGE,"E34");var subQ1=sQuery(id+"F5.wireOp",EDGE,"E13");var subQ2=makeQuery(id+"F5.imprint","INTERSECT",VERTEX,{"disambiguationData":[OD(0.0)],"derivedFrom":[subQ1,subQ0]});Q7=makeQuery(id+"F5.imprint","IMPRINT",FACE,{"disambiguationData":[TD([[makeQuery(id+"F5.imprint","IMPRINT",EDGE,{"disambiguationData":[TD([[subQ2,-1.0]])],"derivedFrom":subQ1}),-1.0]])]});}
            var Q8;
            {var subQ1=sQuery(id+"F5.wireOp",EDGE,"E36.bottom");Q8=makeQuery(id+"F5.imprint","IMPRINT",FACE,{"disambiguationData":[TD([[makeQuery(id+"F5.imprint","IMPRINT",EDGE,{"derivedFrom":subQ1}),-1.0]])]});}
            var Q9;
            {var subQ0=sQuery(id+"F5.wireOp",EDGE,"E36.top");var subQ1=sQuery(id+"F5.wireOp",EDGE,"E13");var subQ2=makeQuery(id+"F5.imprint","INTERSECT",VERTEX,{"derivedFrom":[subQ1,subQ0]});Q9=makeQuery(id+"F5.imprint","IMPRINT",FACE,{"disambiguationData":[TD([[makeQuery(id+"F5.imprint","IMPRINT",EDGE,{"disambiguationData":[TD([[subQ2,-1.0]])],"derivedFrom":subQ1}),1.0]])]});}
            var Q10;
            {var subQ0=sQuery(id+"F5.wireOp",EDGE,"E35");var subQ1=sQuery(id+"F5.wireOp",EDGE,"E13");var subQ2=makeQuery(id+"F5.imprint","INTERSECT",VERTEX,{"disambiguationData":[OD(0.0)],"derivedFrom":[subQ1,subQ0]});Q10=makeQuery(id+"F5.imprint","IMPRINT",FACE,{"disambiguationData":[TD([[makeQuery(id+"F5.imprint","IMPRINT",EDGE,{"disambiguationData":[TD([[subQ2,-1.0]])],"derivedFrom":subQ1}),-1.0]])]});}
            var Q11;
            {var subQ0=sQuery(id+"F5.wireOp",EDGE,"E35");var subQ1=sQuery(id+"F5.wireOp",EDGE,"E13");var subQ2=makeQuery(id+"F5.imprint","INTERSECT",VERTEX,{"disambiguationData":[OD(0.0)],"derivedFrom":[subQ1,subQ0]});Q11=makeQuery(id+"F5.imprint","IMPRINT",FACE,{"disambiguationData":[TD([[makeQuery(id+"F5.imprint","IMPRINT",EDGE,{"disambiguationData":[TD([[subQ2,-1.0]])],"derivedFrom":subQ1}),1.0]])]});}
            extrude(context, id + "F9", {"entities" : qUnion([Q0, Q1, Q2, Q3, Q4, Q5, Q6, Q7, Q8, Q9, Q10, Q11]), "operationType" : NewBodyOperationType.ADD, "depth" : 8 * mm, "offsetDistance" : 25 * mm});
        }
        {
            var Q0;
            Q0=makeQuery(id+"F9.opExtrude","CAP_EDGE",EDGE,{"disambiguationData":[OSD([sQuery(id+"F5.wireOp",EDGE,"E35")])],"isStart":false});
            var Q1;
            Q1=makeQuery(id+"F9.opExtrude","CAP_FACE",FACE,{"disambiguationData":[OSD([sQuery(id+"F5.wireOp",EDGE,"E31")])],"isStart":false});
            var Q2;
            Q2=makeQuery(id+"F9.opExtrude","CAP_FACE",FACE,{"disambiguationData":[OSD([sQuery(id+"F5.wireOp",EDGE,"E32")])],"isStart":false});
            var Q3;
            Q3=makeQuery(id+"F9.opExtrude","CAP_FACE",FACE,{"disambiguationData":[OSD([sQuery(id+"F5.wireOp",EDGE,"E33")])],"isStart":false});
            var Q4;
            Q4=makeQuery(id+"F9.opExtrude","CAP_FACE",FACE,{"disambiguationData":[OSD([sQuery(id+"F5.wireOp",EDGE,"E34")])],"isStart":false});
            var Q5;
            Q5=makeQuery(id+"F9.opExtrude","CAP_EDGE",EDGE,{"disambiguationData":[OSD([sQuery(id+"F5.wireOp",EDGE,"E36.left")])],"isStart":false});
            var Q6;
            Q6=makeQuery(id+"F9.opExtrude","CAP_EDGE",EDGE,{"disambiguationData":[OSD([sQuery(id+"F5.wireOp",EDGE,"E36.right")])],"isStart":false});
            var Q7;
            Q7=makeQuery(id+"F9.opExtrude","CAP_EDGE",EDGE,{"disambiguationData":[OSD([sQuery(id+"F5.wireOp",EDGE,"E36.bottom")])],"isStart":false});
            var Q8;
            Q8=makeQuery(id+"F9.opExtrude","CAP_EDGE",EDGE,{"disambiguationData":[OSD([sQuery(id+"F5.wireOp",EDGE,"E36.top")])],"isStart":false});
            fillet(context, id + "F10", {"entities" : qUnion([Q0, Q1, Q2, Q3, Q4, Q5, Q6, Q7, Q8]), "radius" : .45 * mm, "tangentPropagation" : true, "allowEdgeOverflow" : false});
        }
        {
            var Q0;
            {var subQ0=sQuery(id+"F5.wireOp",EDGE,"E35");var subQ1=sQuery(id+"F5.wireOp",EDGE,"E13");var subQ2=makeQuery(id+"F5.imprint","INTERSECT",VERTEX,{"disambiguationData":[OD(0.0)],"derivedFrom":[subQ1,subQ0]});Q0=makeQuery(id+"F5.imprint","IMPRINT",FACE,{"disambiguationData":[TD([[makeQuery(id+"F5.imprint","IMPRINT",EDGE,{"disambiguationData":[TD([[subQ2,-1.0]])],"derivedFrom":subQ1}),-1.0]])]});}
            var Q1;
            {var subQ0=sQuery(id+"F5.wireOp",EDGE,"E35");var subQ1=sQuery(id+"F5.wireOp",EDGE,"E13");var subQ2=makeQuery(id+"F5.imprint","INTERSECT",VERTEX,{"disambiguationData":[OD(0.0)],"derivedFrom":[subQ1,subQ0]});Q1=makeQuery(id+"F5.imprint","IMPRINT",FACE,{"disambiguationData":[TD([[makeQuery(id+"F5.imprint","IMPRINT",EDGE,{"disambiguationData":[TD([[subQ2,-1.0]])],"derivedFrom":subQ1}),1.0]])]});}
            var Q2;
            {var subQ1=sQuery(id+"F5.wireOp",EDGE,"E36.bottom");Q2=makeQuery(id+"F5.imprint","IMPRINT",FACE,{"disambiguationData":[TD([[makeQuery(id+"F5.imprint","IMPRINT",EDGE,{"derivedFrom":subQ1}),-1.0]])]});}
            var Q3;
            {var subQ0=sQuery(id+"F5.wireOp",EDGE,"E36.top");var subQ1=sQuery(id+"F5.wireOp",EDGE,"E13");var subQ2=makeQuery(id+"F5.imprint","INTERSECT",VERTEX,{"derivedFrom":[subQ1,subQ0]});Q3=makeQuery(id+"F5.imprint","IMPRINT",FACE,{"disambiguationData":[TD([[makeQuery(id+"F5.imprint","IMPRINT",EDGE,{"disambiguationData":[TD([[subQ2,-1.0]])],"derivedFrom":subQ1}),1.0]])]});}
            var Q4;
            {var subQ0=sQuery(id+"F5.wireOp",EDGE,"E34");var subQ1=sQuery(id+"F5.wireOp",EDGE,"E13");var subQ2=makeQuery(id+"F5.imprint","INTERSECT",VERTEX,{"disambiguationData":[OD(0.0)],"derivedFrom":[subQ1,subQ0]});Q4=makeQuery(id+"F5.imprint","IMPRINT",FACE,{"disambiguationData":[TD([[makeQuery(id+"F5.imprint","IMPRINT",EDGE,{"disambiguationData":[TD([[subQ2,-1.0]])],"derivedFrom":subQ1}),1.0]])]});}
            var Q5;
            {var subQ0=sQuery(id+"F5.wireOp",EDGE,"E34");var subQ1=sQuery(id+"F5.wireOp",EDGE,"E13");var subQ2=makeQuery(id+"F5.imprint","INTERSECT",VERTEX,{"disambiguationData":[OD(0.0)],"derivedFrom":[subQ1,subQ0]});Q5=makeQuery(id+"F5.imprint","IMPRINT",FACE,{"disambiguationData":[TD([[makeQuery(id+"F5.imprint","IMPRINT",EDGE,{"disambiguationData":[TD([[subQ2,-1.0]])],"derivedFrom":subQ1}),-1.0]])]});}
            var Q6;
            {var subQ0=sQuery(id+"F5.wireOp",EDGE,"E33");var subQ1=sQuery(id+"F5.wireOp",EDGE,"E13");var subQ2=makeQuery(id+"F5.imprint","INTERSECT",VERTEX,{"disambiguationData":[OD(0.0)],"derivedFrom":[subQ1,subQ0]});Q6=makeQuery(id+"F5.imprint","IMPRINT",FACE,{"disambiguationData":[TD([[makeQuery(id+"F5.imprint","IMPRINT",EDGE,{"disambiguationData":[TD([[subQ2,-1.0]])],"derivedFrom":subQ1}),1.0]])]});}
            var Q7;
            {var subQ0=sQuery(id+"F5.wireOp",EDGE,"E33");var subQ1=sQuery(id+"F5.wireOp",EDGE,"E13");var subQ2=makeQuery(id+"F5.imprint","INTERSECT",VERTEX,{"disambiguationData":[OD(0.0)],"derivedFrom":[subQ1,subQ0]});Q7=makeQuery(id+"F5.imprint","IMPRINT",FACE,{"disambiguationData":[TD([[makeQuery(id+"F5.imprint","IMPRINT",EDGE,{"disambiguationData":[TD([[subQ2,-1.0]])],"derivedFrom":subQ1}),-1.0]])]});}
            var Q8;
            {var subQ0=sQuery(id+"F5.wireOp",EDGE,"E32");var subQ1=sQuery(id+"F5.wireOp",EDGE,"E13");var subQ2=makeQuery(id+"F5.imprint","INTERSECT",VERTEX,{"disambiguationData":[OD(0.0)],"derivedFrom":[subQ1,subQ0]});Q8=makeQuery(id+"F5.imprint","IMPRINT",FACE,{"disambiguationData":[TD([[makeQuery(id+"F5.imprint","IMPRINT",EDGE,{"disambiguationData":[TD([[subQ2,-1.0]])],"derivedFrom":subQ1}),1.0]])]});}
            var Q9;
            {var subQ0=sQuery(id+"F5.wireOp",EDGE,"E32");var subQ1=sQuery(id+"F5.wireOp",EDGE,"E13");var subQ2=makeQuery(id+"F5.imprint","INTERSECT",VERTEX,{"disambiguationData":[OD(0.0)],"derivedFrom":[subQ1,subQ0]});Q9=makeQuery(id+"F5.imprint","IMPRINT",FACE,{"disambiguationData":[TD([[makeQuery(id+"F5.imprint","IMPRINT",EDGE,{"disambiguationData":[TD([[subQ2,-1.0]])],"derivedFrom":subQ1}),-1.0]])]});}
            var Q10;
            {var subQ0=sQuery(id+"F5.wireOp",EDGE,"E31");var subQ1=sQuery(id+"F5.wireOp",EDGE,"E13");var subQ2=makeQuery(id+"F5.imprint","INTERSECT",VERTEX,{"disambiguationData":[OD(0.0)],"derivedFrom":[subQ1,subQ0]});Q10=makeQuery(id+"F5.imprint","IMPRINT",FACE,{"disambiguationData":[TD([[makeQuery(id+"F5.imprint","IMPRINT",EDGE,{"disambiguationData":[TD([[subQ2,-1.0]])],"derivedFrom":subQ1}),-1.0]])]});}
            var Q11;
            {var subQ0=sQuery(id+"F5.wireOp",EDGE,"E31");var subQ1=sQuery(id+"F5.wireOp",EDGE,"E13");var subQ2=makeQuery(id+"F5.imprint","INTERSECT",VERTEX,{"disambiguationData":[OD(0.0)],"derivedFrom":[subQ1,subQ0]});Q11=makeQuery(id+"F5.imprint","IMPRINT",FACE,{"disambiguationData":[TD([[makeQuery(id+"F5.imprint","IMPRINT",EDGE,{"disambiguationData":[TD([[subQ2,-1.0]])],"derivedFrom":subQ1}),1.0]])]});}
            extrude(context, id + "F11", {"entities" : qUnion([Q0, Q1, Q2, Q3, Q4, Q5, Q6, Q7, Q8, Q9, Q10, Q11]), "operationType" : NewBodyOperationType.REMOVE, "depth" : 1.8 * mm, "offsetDistance" : 25 * mm});
        }
        {
            var Q0;
            Q0=qCreatedBy(makeId("Top.planeOp"),FACE);
            var sketch = newSketch(context, id + "F12", { "sketchPlane" : qUnion([Q0])});
            skCircle(sketch, "E37", {"center": v(0, 0) * mm, "radius": 13.47 * mm});
            skSolve(sketch);
        }
        {
            var Q0;
            Q0=makeQuery(id+"F12.imprint","IMPRINT",FACE,{"disambiguationData":[TD([[makeQuery(id+"F12.imprint","IMPRINT",EDGE,{"derivedFrom":sQuery(id+"F12.wireOp",EDGE,"E37")}),1.0]])]});
            extrude(context, id + "F13", {"entities" : qUnion([Q0]), "operationType" : NewBodyOperationType.REMOVE, "depth" : 1 * mm, "offsetDistance" : 25 * mm});
        }
        {
            var Q0;
            {var subQ0=sQuery(id+"F0.wireOp",EDGE,"E8.right");var subQ1=sQuery(id+"F0.wireOp",EDGE,"E1.0");var subQ2=makeQuery(id+"F0.imprint","INTERSECT",VERTEX,{"disambiguationData":[OD(1.0)],"derivedFrom":[subQ1,subQ0]});Q0=makeQuery(id+"F0.imprint","IMPRINT",FACE,{"disambiguationData":[TD([[makeQuery(id+"F0.imprint","IMPRINT",EDGE,{"disambiguationData":[TD([[subQ2,-1.0]])],"derivedFrom":subQ1}),1.0]])]});}
            var Q1;
            {var subQ0=sQuery(id+"F0.wireOp",EDGE,"E3.right");var subQ1=sQuery(id+"F0.wireOp",EDGE,"E1.0");var subQ2=makeQuery(id+"F0.imprint","INTERSECT",VERTEX,{"disambiguationData":[OD(0.0)],"derivedFrom":[subQ1,subQ0]});Q1=makeQuery(id+"F0.imprint","IMPRINT",FACE,{"disambiguationData":[TD([[makeQuery(id+"F0.imprint","IMPRINT",EDGE,{"disambiguationData":[TD([[subQ2,1.0]])],"derivedFrom":subQ1}),1.0]])]});}
            var Q2;
            {var subQ0=sQuery(id+"F0.wireOp",EDGE,"E3.left");var subQ1=sQuery(id+"F0.wireOp",EDGE,"E1.0");var subQ2=makeQuery(id+"F0.imprint","INTERSECT",VERTEX,{"disambiguationData":[OD(0.0)],"derivedFrom":[subQ1,subQ0]});Q2=makeQuery(id+"F0.imprint","IMPRINT",FACE,{"disambiguationData":[TD([[makeQuery(id+"F0.imprint","IMPRINT",EDGE,{"disambiguationData":[TD([[subQ2,-1.0]])],"derivedFrom":subQ1}),1.0]])]});}
            var Q3;
            {var subQ0=sQuery(id+"F0.wireOp",EDGE,"E2.left");var subQ1=sQuery(id+"F0.wireOp",EDGE,"E1.0");var subQ2=makeQuery(id+"F0.imprint","INTERSECT",VERTEX,{"disambiguationData":[OD(0.0)],"derivedFrom":[subQ1,subQ0]});Q3=makeQuery(id+"F0.imprint","IMPRINT",FACE,{"disambiguationData":[TD([[makeQuery(id+"F0.imprint","IMPRINT",EDGE,{"disambiguationData":[TD([[subQ2,-1.0]])],"derivedFrom":subQ1}),1.0]])]});}
            var Q4;
            {var subQ0=sQuery(id+"F0.wireOp",EDGE,"E8.left");var subQ1=sQuery(id+"F0.wireOp",EDGE,"E1.0");var subQ2=makeQuery(id+"F0.imprint","INTERSECT",VERTEX,{"disambiguationData":[OD(0.0)],"derivedFrom":[subQ1,subQ0]});Q4=makeQuery(id+"F0.imprint","IMPRINT",FACE,{"disambiguationData":[TD([[makeQuery(id+"F0.imprint","IMPRINT",EDGE,{"disambiguationData":[TD([[subQ2,-1.0]])],"derivedFrom":subQ1}),1.0]])]});}
            var Q5;
            {var subQ0=sQuery(id+"F0.wireOp",EDGE,"E3.right");var subQ1=sQuery(id+"F0.wireOp",EDGE,"E1.0");var subQ2=makeQuery(id+"F0.imprint","INTERSECT",VERTEX,{"disambiguationData":[OD(1.0)],"derivedFrom":[subQ1,subQ0]});Q5=makeQuery(id+"F0.imprint","IMPRINT",FACE,{"disambiguationData":[TD([[makeQuery(id+"F0.imprint","IMPRINT",EDGE,{"disambiguationData":[TD([[subQ2,-1.0]])],"derivedFrom":subQ1}),1.0]])]});}
            var Q6;
            {var subQ0=sQuery(id+"F0.wireOp",EDGE,"E2.right");var subQ1=sQuery(id+"F0.wireOp",EDGE,"E1.0");var subQ2=makeQuery(id+"F0.imprint","INTERSECT",VERTEX,{"disambiguationData":[OD(1.0)],"derivedFrom":[subQ1,subQ0]});Q6=makeQuery(id+"F0.imprint","IMPRINT",FACE,{"disambiguationData":[TD([[makeQuery(id+"F0.imprint","IMPRINT",EDGE,{"disambiguationData":[TD([[subQ2,-1.0]])],"derivedFrom":subQ1}),1.0]])]});}
            extrude(context, id + "F14", {"entities" : qUnion([Q0, Q1, Q2, Q3, Q4, Q5, Q6]), "operationType" : NewBodyOperationType.REMOVE, "depth" : 1 * mm, "offsetDistance" : 25 * mm});
        }
        {
            var Q0;
            Q0=makeQuery(id+"F14.boolean.opBoolean","COPY",EDGE,{"derivedFrom":makeQuery(id+"F14.opExtrude","SWEPT_EDGE",EDGE,{"disambiguationData":[OSD([sQuery(id+"F0.wireOp",EDGE,"E1.0"),sQuery(id+"F0.wireOp",EDGE,"E9.right")])]})});
            var Q1;
            {var subQ0=sQuery(id+"F0.wireOp",EDGE,"E8.right");var subQ1=sQuery(id+"F0.wireOp",EDGE,"E1.0");Q1=makeQuery(id+"F14.boolean.opBoolean","COPY",EDGE,{"derivedFrom":makeQuery(id+"F14.opExtrude","SWEPT_EDGE",EDGE,{"disambiguationData":[OSD([subQ1,subQ0]),TDD([makeQuery(id+"F0.imprint","INTERSECT",VERTEX,{"disambiguationData":[OD(0.0)],"derivedFrom":[subQ1,subQ0]})])]})});}
            var Q2;
            {var subQ0=sQuery(id+"F0.wireOp",EDGE,"E8.left");var subQ1=sQuery(id+"F0.wireOp",EDGE,"E1.0");Q2=makeQuery(id+"F14.boolean.opBoolean","COPY",EDGE,{"derivedFrom":makeQuery(id+"F14.opExtrude","SWEPT_EDGE",EDGE,{"disambiguationData":[OSD([subQ1,subQ0]),TDD([makeQuery(id+"F0.imprint","INTERSECT",VERTEX,{"disambiguationData":[OD(0.0)],"derivedFrom":[subQ1,subQ0]})])]})});}
            var Q3;
            {var subQ0=sQuery(id+"F0.wireOp",EDGE,"E2.left");var subQ1=sQuery(id+"F0.wireOp",EDGE,"E1.0");Q3=makeQuery(id+"F14.boolean.opBoolean","COPY",EDGE,{"derivedFrom":makeQuery(id+"F14.opExtrude","SWEPT_EDGE",EDGE,{"disambiguationData":[OSD([subQ1,subQ0]),TDD([makeQuery(id+"F0.imprint","INTERSECT",VERTEX,{"disambiguationData":[OD(0.0)],"derivedFrom":[subQ1,subQ0]})])]})});}
            var Q4;
            {var subQ0=sQuery(id+"F0.wireOp",EDGE,"E2.right");var subQ1=sQuery(id+"F0.wireOp",EDGE,"E1.0");Q4=makeQuery(id+"F14.boolean.opBoolean","COPY",EDGE,{"derivedFrom":makeQuery(id+"F14.opExtrude","SWEPT_EDGE",EDGE,{"disambiguationData":[OSD([subQ1,subQ0]),TDD([makeQuery(id+"F0.imprint","INTERSECT",VERTEX,{"disambiguationData":[OD(0.0)],"derivedFrom":[subQ1,subQ0]})])]})});}
            var Q5;
            {var subQ0=sQuery(id+"F0.wireOp",EDGE,"E3.right");var subQ1=sQuery(id+"F0.wireOp",EDGE,"E1.0");Q5=makeQuery(id+"F14.boolean.opBoolean","COPY",EDGE,{"derivedFrom":makeQuery(id+"F14.opExtrude","SWEPT_EDGE",EDGE,{"disambiguationData":[OSD([subQ1,subQ0]),TDD([makeQuery(id+"F0.imprint","INTERSECT",VERTEX,{"disambiguationData":[OD(0.0)],"derivedFrom":[subQ1,subQ0]})])]})});}
            var Q6;
            Q6=makeQuery(id+"F14.boolean.opBoolean","COPY",EDGE,{"derivedFrom":makeQuery(id+"F14.opExtrude","SWEPT_EDGE",EDGE,{"disambiguationData":[OSD([sQuery(id+"F0.wireOp",EDGE,"E1.0"),sQuery(id+"F0.wireOp",EDGE,"E3.left")])]})});
            var Q7;
            Q7=makeQuery(id+"F14.boolean.opBoolean","COPY",EDGE,{"derivedFrom":makeQuery(id+"F14.opExtrude","SWEPT_EDGE",EDGE,{"disambiguationData":[OSD([sQuery(id+"F0.wireOp",EDGE,"E1.0"),sQuery(id+"F0.wireOp",EDGE,"E6.bottom")])]})});
            var Q8;
            {var subQ0=sQuery(id+"F0.wireOp",EDGE,"E3.right");var subQ1=sQuery(id+"F0.wireOp",EDGE,"E1.0");Q8=makeQuery(id+"F14.boolean.opBoolean","COPY",EDGE,{"derivedFrom":makeQuery(id+"F14.opExtrude","SWEPT_EDGE",EDGE,{"disambiguationData":[OSD([subQ1,subQ0]),TDD([makeQuery(id+"F0.imprint","INTERSECT",VERTEX,{"disambiguationData":[OD(1.0)],"derivedFrom":[subQ1,subQ0]})])]})});}
            var Q9;
            {var subQ0=sQuery(id+"F0.wireOp",EDGE,"E8.right");var subQ1=sQuery(id+"F0.wireOp",EDGE,"E1.0");Q9=makeQuery(id+"F14.boolean.opBoolean","COPY",EDGE,{"derivedFrom":makeQuery(id+"F14.opExtrude","SWEPT_EDGE",EDGE,{"disambiguationData":[OSD([subQ1,subQ0]),TDD([makeQuery(id+"F0.imprint","INTERSECT",VERTEX,{"disambiguationData":[OD(1.0)],"derivedFrom":[subQ1,subQ0]})])]})});}
            var Q10;
            {var subQ0=sQuery(id+"F0.wireOp",EDGE,"E2.right");var subQ1=sQuery(id+"F0.wireOp",EDGE,"E1.0");Q10=makeQuery(id+"F14.boolean.opBoolean","COPY",EDGE,{"derivedFrom":makeQuery(id+"F14.opExtrude","SWEPT_EDGE",EDGE,{"disambiguationData":[OSD([subQ1,subQ0]),TDD([makeQuery(id+"F0.imprint","INTERSECT",VERTEX,{"disambiguationData":[OD(1.0)],"derivedFrom":[subQ1,subQ0]})])]})});}
            var Q11;
            {var subQ0=sQuery(id+"F0.wireOp",EDGE,"E8.left");var subQ1=sQuery(id+"F0.wireOp",EDGE,"E1.0");Q11=makeQuery(id+"F14.boolean.opBoolean","COPY",EDGE,{"derivedFrom":makeQuery(id+"F14.opExtrude","SWEPT_EDGE",EDGE,{"disambiguationData":[OSD([subQ1,subQ0]),TDD([makeQuery(id+"F0.imprint","INTERSECT",VERTEX,{"disambiguationData":[OD(1.0)],"derivedFrom":[subQ1,subQ0]})])]})});}
            var Q12;
            {var subQ0=sQuery(id+"F0.wireOp",EDGE,"E2.left");var subQ1=sQuery(id+"F0.wireOp",EDGE,"E1.0");Q12=makeQuery(id+"F14.boolean.opBoolean","COPY",EDGE,{"derivedFrom":makeQuery(id+"F14.opExtrude","SWEPT_EDGE",EDGE,{"disambiguationData":[OSD([subQ1,subQ0]),TDD([makeQuery(id+"F0.imprint","INTERSECT",VERTEX,{"disambiguationData":[OD(1.0)],"derivedFrom":[subQ1,subQ0]})])]})});}
            var Q13;
            Q13=makeQuery(id+"F14.boolean.opBoolean","COPY",EDGE,{"derivedFrom":makeQuery(id+"F14.opExtrude","SWEPT_EDGE",EDGE,{"disambiguationData":[OSD([sQuery(id+"F0.wireOp",EDGE,"E1.0"),sQuery(id+"F0.wireOp",EDGE,"E9.left")])]})});
            fillet(context, id + "F15", {"entities" : qUnion([Q0, Q1, Q2, Q3, Q4, Q5, Q6, Q7, Q8, Q9, Q10, Q11, Q12, Q13]), "radius" : 1 * mm, "tangentPropagation" : true, "allowEdgeOverflow" : false});
        }
    });
